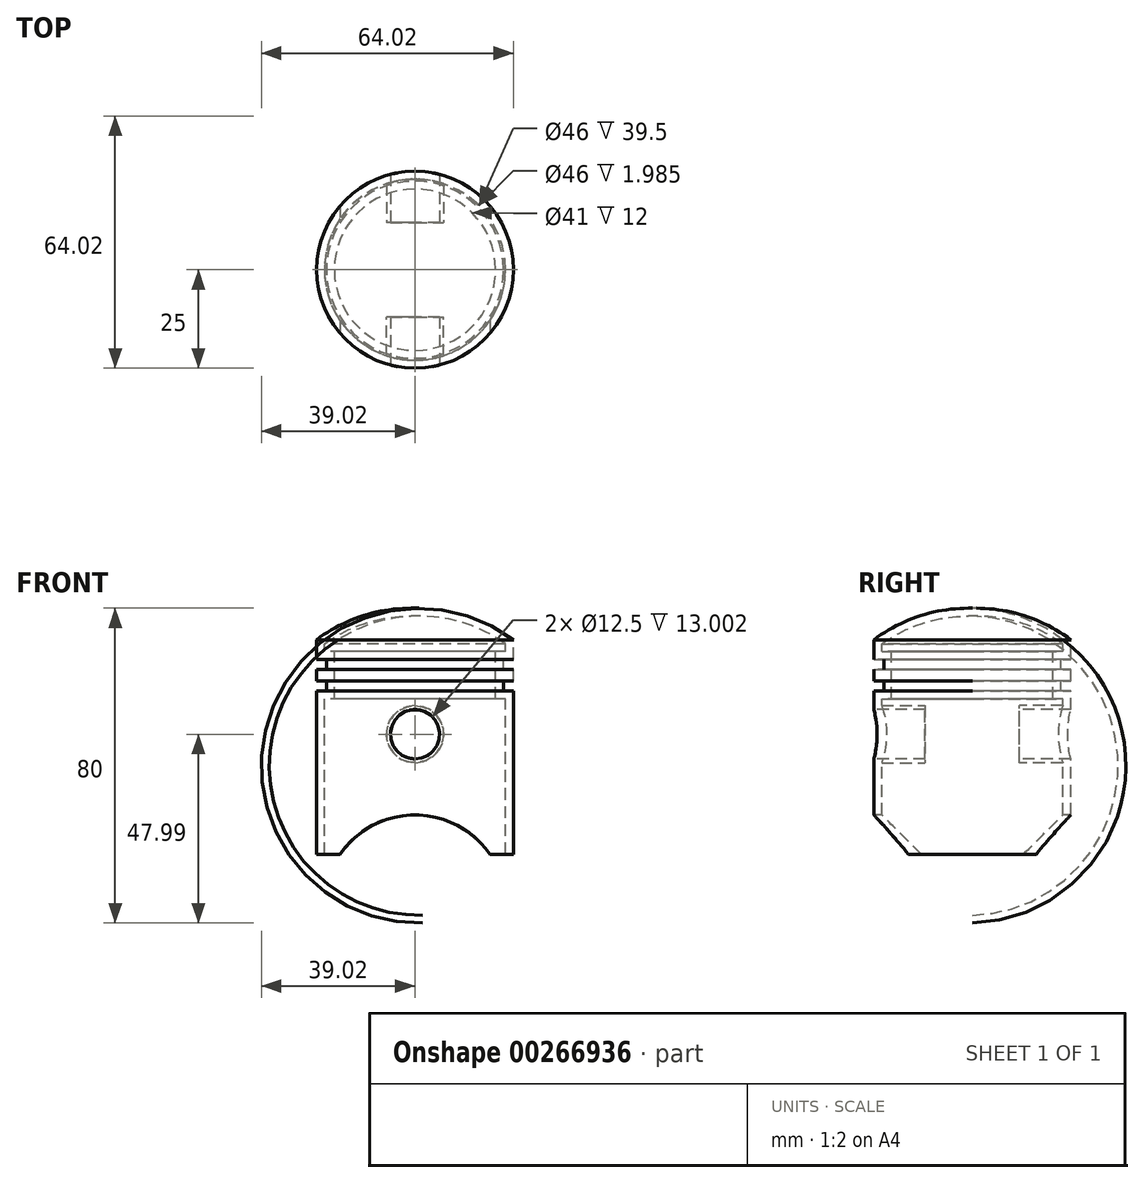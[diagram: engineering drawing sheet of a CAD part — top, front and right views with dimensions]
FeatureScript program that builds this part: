
annotation { "Feature Type Name" : "Feature", "Feature Type Description" : "" }
export const myFeature = defineFeature(function(context is Context, id is Id, definition is map)
    precondition{}
    {
        {
            var Q0;
            Q0=qCreatedBy(makeId("Front.planeOp"),FACE);
            var sketch = newSketch(context, id + "F0", { "sketchPlane" : qUnion([Q0])});
            skLineSegment(sketch, "E0", {"start": v(-12.5, 62.5) * mm, "end": v(-12.5, 60.5) * mm});
            skLineSegment(sketch, "E1", {"start": v(10.5, 0) * mm, "end": v(12.5, 0) * mm});
            skLineSegment(sketch, "E2", {"start": v(12.5, 0) * mm, "end": v(12.5, 41.5) * mm});
            skLineSegment(sketch, "E3", {"start": v(12.5, 41.5) * mm, "end": v(10, 41.5) * mm});
            skLineSegment(sketch, "E4", {"start": v(10, 41.5) * mm, "end": v(10, 44) * mm});
            skLineSegment(sketch, "E5", {"start": v(10, 44) * mm, "end": v(12.5, 44) * mm});
            skLineSegment(sketch, "E6", {"start": v(12.5, 44) * mm, "end": v(12.5, 47) * mm});
            skLineSegment(sketch, "E7", {"start": v(12.5, 47) * mm, "end": v(10, 47) * mm});
            skLineSegment(sketch, "E8", {"start": v(10, 47) * mm, "end": v(10, 49.5) * mm});
            skLineSegment(sketch, "E9", {"start": v(10, 49.5) * mm, "end": v(12.5, 49.5) * mm});
            skLineSegment(sketch, "E10", {"start": v(12.5, 49.5) * mm, "end": v(12.5, 54.5) * mm});
            skArc(sketch, "E11", {"start": v(12.5, 54.5) * mm, "mid": v(0.67, 60.6) * mm, "end": v(-12.5, 62.5) * mm});
            skLineSegment(sketch, "E12.1", {"start": v(8, 43.4) * mm, "end": v(8, 51.5) * mm});
            skLineSegment(sketch, "E12.3", {"start": v(8, 39.5) * mm, "end": v(8, 43.4) * mm});
            skLineSegment(sketch, "E12.6", {"start": v(10.5, 0) * mm, "end": v(10.5, 39.5) * mm});
            skLineSegment(sketch, "E12.7", {"start": v(10.5, 39.5) * mm, "end": v(8, 39.5) * mm});
            skArc(sketch, "E13.0", {"start": v(10.5, 53.48) * mm, "mid": v(-0.43, 58.86) * mm, "end": v(-12.5, 60.5) * mm});
            skLineSegment(sketch, "E14.0", {"start": v(10.5, 51.5) * mm, "end": v(10.5, 53.48) * mm});
            skLineSegment(sketch, "E14.1", {"start": v(10, 51.5) * mm, "end": v(10.5, 51.5) * mm});
            skLineSegment(sketch, "E15", {"start": v(8, 51.5) * mm, "end": v(10, 51.5) * mm});
            skPoint(sketch, "E16.orphan", {"position": v(-12.5, 0) * mm});
            skSolve(sketch);
        }
        {
            var Q0;
            Q0=makeQuery(id+"F0.imprint","IMPRINT",FACE,{"disambiguationData":[TD([[makeQuery(id+"F0.imprint","IMPRINT",EDGE,{"derivedFrom":sQuery(id+"F0.wireOp",EDGE,"E0")}),1.0]])]});
            var Q1;
            Q1=sQuery(id+"F0.wireOp",EDGE,"E0");
            revolve(context, id + "F1", {"entities" : qUnion([Q0]), "axis" : qUnion([Q1]), "revolveType" : RevolveType.FULL});
        }
        {
            var Q0;
            Q0=qCreatedBy(makeId("Front.planeOp"),FACE);
            var sketch = newSketch(context, id + "F2", { "sketchPlane" : qUnion([Q0])});
            skLineSegment(sketch, "E17.0", {"start": v(-31.5, 0) * mm, "end": v(6.5, 0) * mm});
            skLineSegment(sketch, "E18", {"start": v(-12.5, 79.25) * mm, "end": v(-12.5, -20.14) * mm, "construction": true});
            skLineSegment(sketch, "E19", {"start": v(-12.5, 0) * mm, "end": v(-12.5, 10) * mm});
            skArc(sketch, "E20", {"start": v(6.5, 0) * mm, "mid": v(-12.5, 10) * mm, "end": v(-31.5, 0) * mm});
            skPoint(sketch, "E21.orphan", {"position": v(-37.5, 0) * mm});
            skPoint(sketch, "E22.orphan", {"position": v(12.5, 0) * mm});
            skCircle(sketch, "E23", {"center": v(-12.5, 30.5) * mm, "radius": 6.25 * mm});
            skPoint(sketch, "E24.0", {"position": v(-12.5, 62.5) * mm});
            skSolve(sketch);
        }
        {
            var Q0;
            Q0 = qSketchRegion(id + "F2", true);
            extrude(context, id + "F3", {"entities" : qUnion([Q0]), "operationType" : NewBodyOperationType.REMOVE, "endBound" : BoundingType.SYMMETRIC, "oppositeDirection" : true, "depth" : 77 * mm});
        }
        {
            var Q0;
            Q0=qCreatedBy(makeId("Front.planeOp"),FACE);
            cPlane(context, id + "F4", {"entities" : qUnion([Q0]), "cplaneType" : CPlaneType.OFFSET, "offset" : 12 * mm, "width" : 150 * mm, "height" : 150 * mm});
        }
        {
            var Q0;
            Q0=qCreatedBy(id+"F4.planeOp",FACE);
            var sketch = newSketch(context, id + "F5", { "sketchPlane" : qUnion([Q0])});
            skCircle(sketch, "E25.0", {"center": v(-12.5, 30.5) * mm, "radius": 6.25 * mm});
            skCircle(sketch, "E26", {"center": v(-12.5, 30.5) * mm, "radius": 7.25 * mm});
            skSolve(sketch);
        }
        {
            var Q0;
            Q0 = qSketchRegion(id + "F5", true);
            extrude(context, id + "F6", {"entities" : qUnion([Q0]), "operationType" : NewBodyOperationType.ADD, "endBound" : BoundingType.UP_TO_NEXT, "depth" : 25 * mm});
        }
        {
            var Q0;
            Q0=makeQuery(id+"F1.opRevolve","SWEPT_BODY",BODY,{"disambiguationData":[OSD([sQuery(id+"F0.wireOp",EDGE,"E0"),sQuery(id+"F0.wireOp",EDGE,"E1"),sQuery(id+"F0.wireOp",EDGE,"E2"),sQuery(id+"F0.wireOp",EDGE,"E3"),sQuery(id+"F0.wireOp",EDGE,"E4"),sQuery(id+"F0.wireOp",EDGE,"E5"),sQuery(id+"F0.wireOp",EDGE,"E6"),sQuery(id+"F0.wireOp",EDGE,"E7"),sQuery(id+"F0.wireOp",EDGE,"E8"),sQuery(id+"F0.wireOp",EDGE,"E9"),sQuery(id+"F0.wireOp",EDGE,"E10"),sQuery(id+"F0.wireOp",EDGE,"E11"),sQuery(id+"F0.wireOp",EDGE,"E12.1"),sQuery(id+"F0.wireOp",EDGE,"E12.3"),sQuery(id+"F0.wireOp",EDGE,"E12.6"),sQuery(id+"F0.wireOp",EDGE,"E12.7"),sQuery(id+"F0.wireOp",EDGE,"E13.0"),sQuery(id+"F0.wireOp",EDGE,"E14.0"),sQuery(id+"F0.wireOp",EDGE,"E14.1"),sQuery(id+"F0.wireOp",EDGE,"E15")])]});
            var Q1;
            Q1=qCreatedBy(makeId("Front.planeOp"),FACE);
            mirror(context, id + "F7", {"operationType" : NewBodyOperationType.ADD, "entities" : qUnion([Q0]), "mirrorPlane" : qUnion([Q1])});
        }
    });
